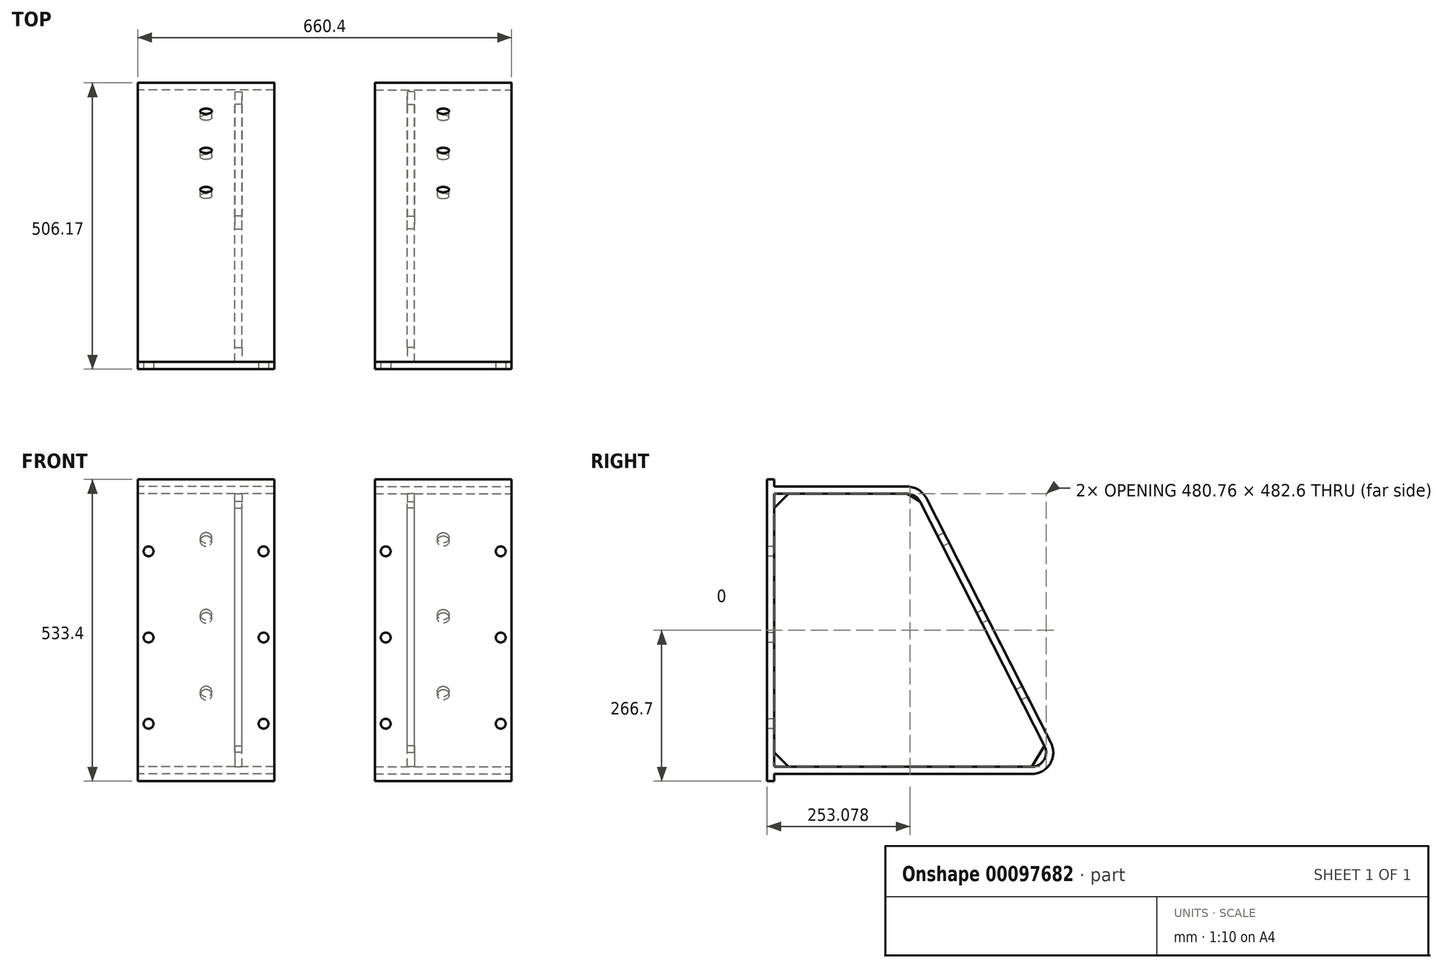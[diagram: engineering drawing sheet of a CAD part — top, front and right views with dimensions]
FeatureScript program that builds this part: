
annotation { "Feature Type Name" : "Feature", "Feature Type Description" : "" }
export const myFeature = defineFeature(function(context is Context, id is Id, definition is map)
    precondition{}
    {
        {
            var Q0;
            Q0=qCreatedBy(makeId("Right.planeOp"),FACE);
            var sketch = newSketch(context, id + "F0", { "sketchPlane" : qUnion([Q0])});
            skLineSegment(sketch, "E0.bottom", {"start": v(0, 0) * mm, "end": v(496.82, 0) * mm});
            skLineSegment(sketch, "E0.top", {"start": v(0, 482.6) * mm, "end": v(250.93, 482.6) * mm});
            skLineSegment(sketch, "E0.left", {"start": v(0, 0) * mm, "end": v(0, 482.6) * mm});
            skLineSegment(sketch, "E1", {"start": v(496.82, 0) * mm, "end": v(250.93, 482.6) * mm});
            skSolve(sketch);
        }
        {
            var Q0;
            Q0=qSketchRegion(id+"F0",true);
            extrude(context, id + "F1", {"entities" : qUnion([Q0]), "endBound" : BoundingType.SYMMETRIC, "depth" : 12.7 * mm});
        }
        {
            var Q0;
            Q0=makeQuery(id+"F1.opExtrude","SWEPT_EDGE",EDGE,{"disambiguationData":[OSD([sQuery(id+"F0.wireOp",EDGE,"E0.top"),sQuery(id+"F0.wireOp",EDGE,"E1")])]});
            var Q1;
            Q1=makeQuery(id+"F1.opExtrude","SWEPT_EDGE",EDGE,{"disambiguationData":[OSD([sQuery(id+"F0.wireOp",EDGE,"E0.top"),sQuery(id+"F0.wireOp",EDGE,"E0.left")])]});
            var Q2;
            Q2=makeQuery(id+"F1.opExtrude","SWEPT_EDGE",EDGE,{"disambiguationData":[OSD([sQuery(id+"F0.wireOp",EDGE,"E0.bottom"),sQuery(id+"F0.wireOp",EDGE,"E0.left")])]});
            var Q3;
            Q3=makeQuery(id+"F1.opExtrude","SWEPT_EDGE",EDGE,{"disambiguationData":[OSD([sQuery(id+"F0.wireOp",EDGE,"E0.bottom"),sQuery(id+"F0.wireOp",EDGE,"E1")])]});
            chamfer(context, id + "F2", {"entities" : qUnion([Q0, Q1, Q2, Q3]), "width" : 25.4 * mm, "tangentPropagation" : true});
        }
        {
            var Q0;
            Q0=makeQuery(id+"F1.opExtrude","CAP_FACE",FACE,{"disambiguationData":[OSD([sQuery(id+"F0.wireOp",EDGE,"E0.bottom"),sQuery(id+"F0.wireOp",EDGE,"E0.top"),sQuery(id+"F0.wireOp",EDGE,"E0.left"),sQuery(id+"F0.wireOp",EDGE,"E1")])],"isStart":false});
            cPlane(context, id + "F3", {"entities" : qUnion([Q0]), "cplaneType" : CPlaneType.OFFSET, "offset" : 171.45 * mm, "width" : 152.4 * mm, "height" : 152.4 * mm});
        }
        {
            var Q0;
            Q0=qCreatedBy(id+"F3.planeOp",FACE);
            var sketch = newSketch(context, id + "F4", { "sketchPlane" : qUnion([Q0])});
            skLineSegment(sketch, "E2.0", {"start": v(0, -25.4) * mm, "end": v(0, 508) * mm});
            skLineSegment(sketch, "E3.0", {"start": v(0, 0) * mm, "end": v(455.37, 0) * mm});
            skLineSegment(sketch, "E4.0", {"start": v(478, 36.93) * mm, "end": v(258, 468.73) * mm});
            skLineSegment(sketch, "E5.0", {"start": v(0, 482.6) * mm, "end": v(235.36, 482.6) * mm});
            skPoint(sketch, "E6.orphan", {"position": v(0, 441.15) * mm});
            skPoint(sketch, "E7.orphan", {"position": v(0, 41.45) * mm});
            skPoint(sketch, "E8.orphan", {"position": v(41.45, 0) * mm});
            skLineSegment(sketch, "E9.0", {"start": v(-12.7, -25.4) * mm, "end": v(0, -25.4) * mm});
            skLineSegment(sketch, "E10.0", {"start": v(-12.7, -25.4) * mm, "end": v(-12.7, 508) * mm});
            skLineSegment(sketch, "E11.0", {"start": v(-12.7, 508) * mm, "end": v(0, 508) * mm});
            skPoint(sketch, "E12.orphan", {"position": v(41.45, 482.6) * mm});
            skPoint(sketch, "E13.orphan", {"position": v(225.53, 482.6) * mm});
            skPoint(sketch, "E14.orphan", {"position": v(262.46, 459.97) * mm});
            skPoint(sketch, "E15.orphan", {"position": v(466.12, 60.27) * mm});
            skPoint(sketch, "E16.orphan", {"position": v(429.19, 0) * mm});
            skPoint(sketch, "E17.visualSharp", {"position": v(496.82, 0) * mm});
            skArc(sketch, "E17.filletArc", {"start": v(455.37, 0) * mm, "mid": v(477.03, 12.13) * mm, "end": v(478, 36.93) * mm});
            skArc(sketch, "E18.filletArc", {"start": v(258, 468.73) * mm, "mid": v(248.63, 478.86) * mm, "end": v(235.36, 482.6) * mm});
            skLineSegment(sketch, "E19.0", {"start": v(0, -12.7) * mm, "end": v(455.37, -12.7) * mm});
            skLineSegment(sketch, "E19.1", {"start": v(0, 495.3) * mm, "end": v(235.36, 495.3) * mm});
            skArc(sketch, "E19.2", {"start": v(269.3, 474.5) * mm, "mid": v(255.27, 489.69) * mm, "end": v(235.36, 495.3) * mm});
            skLineSegment(sketch, "E19.3", {"start": v(489.32, 42.7) * mm, "end": v(269.3, 474.5) * mm});
            skArc(sketch, "E19.4", {"start": v(455.37, -12.7) * mm, "mid": v(487.86, 5.5) * mm, "end": v(489.32, 42.7) * mm});
            skSolve(sketch);
        }
        {
            var Q0;
            Q0=qSketchRegion(id+"F4",true);
            extrude(context, id + "F5", {"entities" : qUnion([Q0]), "operationType" : NewBodyOperationType.ADD, "oppositeDirection" : true, "depth" : 241.3 * mm});
        }
        {
            var Q0;
            Q0=makeQuery(id+"F5.opExtrude","SWEPT_FACE",FACE,{"disambiguationData":[OSD([sQuery(id+"F4.wireOp",EDGE,"E10.0")])]});
            var sketch = newSketch(context, id + "F6", { "sketchPlane" : qUnion([Q0])});
            skLineSegment(sketch, "E20.0", {"start": v(-63.5, 482.6) * mm, "end": v(177.8, 482.6) * mm, "construction": true});
            skLineSegment(sketch, "E21.0", {"start": v(-63.5, 508) * mm, "end": v(177.8, 508) * mm, "construction": true});
            skLineSegment(sketch, "E22", {"start": v(57.15, 508) * mm, "end": v(57.15, 76.2) * mm, "construction": true});
            skLineSegment(sketch, "E23.0", {"start": v(-63.5, 381) * mm, "end": v(177.8, 381) * mm, "construction": true});
            skLineSegment(sketch, "E24.0", {"start": v(-63.5, 228.6) * mm, "end": v(177.8, 228.6) * mm, "construction": true});
            skLineSegment(sketch, "E25.0", {"start": v(-63.5, 76.2) * mm, "end": v(177.8, 76.2) * mm, "construction": true});
            skLineSegment(sketch, "E26.0", {"start": v(-44.45, 508) * mm, "end": v(-44.45, 76.2) * mm, "construction": true});
            skLineSegment(sketch, "E27.0", {"start": v(158.75, 508) * mm, "end": v(158.75, 76.2) * mm, "construction": true});
            skPoint(sketch, "E28", {"position": v(-44.45, 381) * mm});
            skPoint(sketch, "E29", {"position": v(-44.45, 228.6) * mm});
            skPoint(sketch, "E30", {"position": v(-44.45, 76.2) * mm});
            skPoint(sketch, "E31", {"position": v(158.75, 76.2) * mm});
            skPoint(sketch, "E32", {"position": v(158.75, 228.6) * mm});
            skPoint(sketch, "E33", {"position": v(158.75, 381) * mm});
            skSolve(sketch);
        }
        {
            var Q0;
            Q0=sQuery(id+"F6.wireOp",VERTEX,"E28");
            var Q1;
            Q1=sQuery(id+"F6.wireOp",VERTEX,"E33");
            var Q2;
            Q2=sQuery(id+"F6.wireOp",VERTEX,"E29");
            var Q3;
            Q3=sQuery(id+"F6.wireOp",VERTEX,"E32");
            var Q4;
            Q4=sQuery(id+"F6.wireOp",VERTEX,"E30");
            var Q5;
            Q5=sQuery(id+"F6.wireOp",VERTEX,"E31");
            var Q6;
            Q6=makeQuery(id+"F1.opExtrude","SWEPT_BODY",BODY,{"disambiguationData":[OSD([sQuery(id+"F0.wireOp",EDGE,"E0.bottom"),sQuery(id+"F0.wireOp",EDGE,"E0.top"),sQuery(id+"F0.wireOp",EDGE,"E0.left"),sQuery(id+"F0.wireOp",EDGE,"E1")])]});
            hole(context, id + "F7", {"style" : HoleStyle.SIMPLE, "endStyle" : HoleEndStyle.BLIND, "holeDiameter" : 17.46 * mm, "holeDepth" : 25.4 * mm, "locations" : qUnion([Q0, Q1, Q2, Q3, Q4, Q5]), "scope" : qUnion([Q6])});
        }
        {
            var Q0;
            Q0=makeQuery(id+"F1.opExtrude","CAP_FACE",FACE,{"disambiguationData":[OSD([sQuery(id+"F0.wireOp",EDGE,"E0.bottom"),sQuery(id+"F0.wireOp",EDGE,"E0.top"),sQuery(id+"F0.wireOp",EDGE,"E0.left"),sQuery(id+"F0.wireOp",EDGE,"E1")])],"isStart":false});
            var sketch = newSketch(context, id + "F8", { "sketchPlane" : qUnion([Q0])});
            skLineSegment(sketch, "E34.0", {"start": v(517.55, -12.7) * mm, "end": v(502.88, 16.08) * mm});
            skLineSegment(sketch, "E35.0", {"start": v(0, -12.7) * mm, "end": v(455.37, -12.7) * mm, "construction": true});
            skPoint(sketch, "E36.orphan", {"position": v(489.32, 42.7) * mm});
            skPoint(sketch, "E37.orphan", {"position": v(455.37, -12.7) * mm});
            skLineSegment(sketch, "E38", {"start": v(502.88, 16.08) * mm, "end": v(490.55, -12.7) * mm});
            skLineSegment(sketch, "E39.trimOffspring", {"start": v(489.32, 42.7) * mm, "end": v(269.3, 474.5) * mm, "construction": true});
            skLineSegment(sketch, "E40.trimOffspring", {"start": v(490.55, -12.7) * mm, "end": v(517.55, -12.7) * mm});
            skSolve(sketch);
        }
        {
            var Q0;
            Q0=makeQuery(id+"F8.imprint","IMPRINT",FACE,{"disambiguationData":[TD([[makeQuery(id+"F8.imprint","IMPRINT",EDGE,{"derivedFrom":sQuery(id+"F8.wireOp",EDGE,"E34.0")}),1.0]])]});
            extrude(context, id + "F9", {"entities" : qUnion([Q0]), "depth" : 25.4 * mm});
        }
        {
            var Q0;
            Q0=makeQuery(id+"F5.opExtrude","SWEPT_FACE",FACE,{"disambiguationData":[OSD([sQuery(id+"F4.wireOp",EDGE,"E19.3")])]});
            var sketch = newSketch(context, id + "F10", { "sketchPlane" : qUnion([Q0])});
            skLineSegment(sketch, "E41.0", {"start": v(-269.39, -246.28) * mm, "end": v(273.48, -246.28) * mm, "construction": true});
            skPoint(sketch, "E42.orphan", {"position": v(-31.75, -246.28) * mm});
            skPoint(sketch, "E43.orphan", {"position": v(-6.35, -246.28) * mm});
            skLineSegment(sketch, "E44", {"start": v(63.5, -222.2) * mm, "end": v(-177.8, -222.2) * mm, "construction": true});
            skLineSegment(sketch, "E45", {"start": v(-57.15, -222.2) * mm, "end": v(-57.15, 496.96) * mm, "construction": true});
            skPoint(sketch, "E45.endSnap0", {"position": v(-57.15, -184.1) * mm});
            skLineSegment(sketch, "E46.0", {"start": v(-269.39, -82.45) * mm, "end": v(273.48, -82.45) * mm, "construction": true});
            skLineSegment(sketch, "E47.0", {"start": v(-269.39, 69.95) * mm, "end": v(273.48, 69.95) * mm, "construction": true});
            skLineSegment(sketch, "E48.0", {"start": v(-269.39, 222.35) * mm, "end": v(273.48, 222.35) * mm, "construction": true});
            skPoint(sketch, "E49", {"position": v(-57.15, 222.35) * mm});
            skPoint(sketch, "E50", {"position": v(-57.15, 69.95) * mm});
            skPoint(sketch, "E51", {"position": v(-57.15, -82.45) * mm});
            skSolve(sketch);
        }
        {
            var Q0;
            Q0=sQuery(id+"F10.wireOp",VERTEX,"E49");
            var Q1;
            Q1=sQuery(id+"F10.wireOp",VERTEX,"E50");
            var Q2;
            Q2=sQuery(id+"F10.wireOp",VERTEX,"E51");
            var Q3;
            Q3=makeQuery(id+"F1.opExtrude","SWEPT_BODY",BODY,{"disambiguationData":[OSD([sQuery(id+"F0.wireOp",EDGE,"E0.bottom"),sQuery(id+"F0.wireOp",EDGE,"E0.top"),sQuery(id+"F0.wireOp",EDGE,"E0.left"),sQuery(id+"F0.wireOp",EDGE,"E1")])]});
            hole(context, id + "F11", {"style" : HoleStyle.SIMPLE, "endStyle" : HoleEndStyle.BLIND, "holeDiameter" : 20.64 * mm, "holeDepth" : 25.4 * mm, "locations" : qUnion([Q0, Q1, Q2]), "scope" : qUnion([Q3])});
        }
        {
            var Q0;
            Q0=makeQuery(id+"F9.opExtrude","SWEPT_BODY",BODY,{"disambiguationData":[OSD([sQuery(id+"F8.wireOp",EDGE,"E34.0"),sQuery(id+"F8.wireOp",EDGE,"E38"),sQuery(id+"F8.wireOp",EDGE,"E40.trimOffspring")])]});
            deleteBodies(context, id + "F12", {"entities" : qUnion([Q0])});
        }
        {
            var Q0;
            Q0=qCreatedBy(makeId("Right.planeOp"),FACE);
            cPlane(context, id + "F13", {"entities" : qUnion([Q0]), "cplaneType" : CPlaneType.OFFSET, "offset" : 152.4 * mm, "oppositeDirection" : true, "width" : 152.4 * mm, "height" : 152.4 * mm});
        }
        {
            var Q0;
            Q0=makeQuery(id+"F1.opExtrude","SWEPT_BODY",BODY,{"disambiguationData":[OSD([sQuery(id+"F0.wireOp",EDGE,"E0.bottom"),sQuery(id+"F0.wireOp",EDGE,"E0.top"),sQuery(id+"F0.wireOp",EDGE,"E0.left"),sQuery(id+"F0.wireOp",EDGE,"E1")])]});
            var Q1;
            Q1=qCreatedBy(id+"F13.planeOp",FACE);
            mirror(context, id + "F14", {"entities" : qUnion([Q0]), "mirrorPlane" : qUnion([Q1])});
        }
    });
